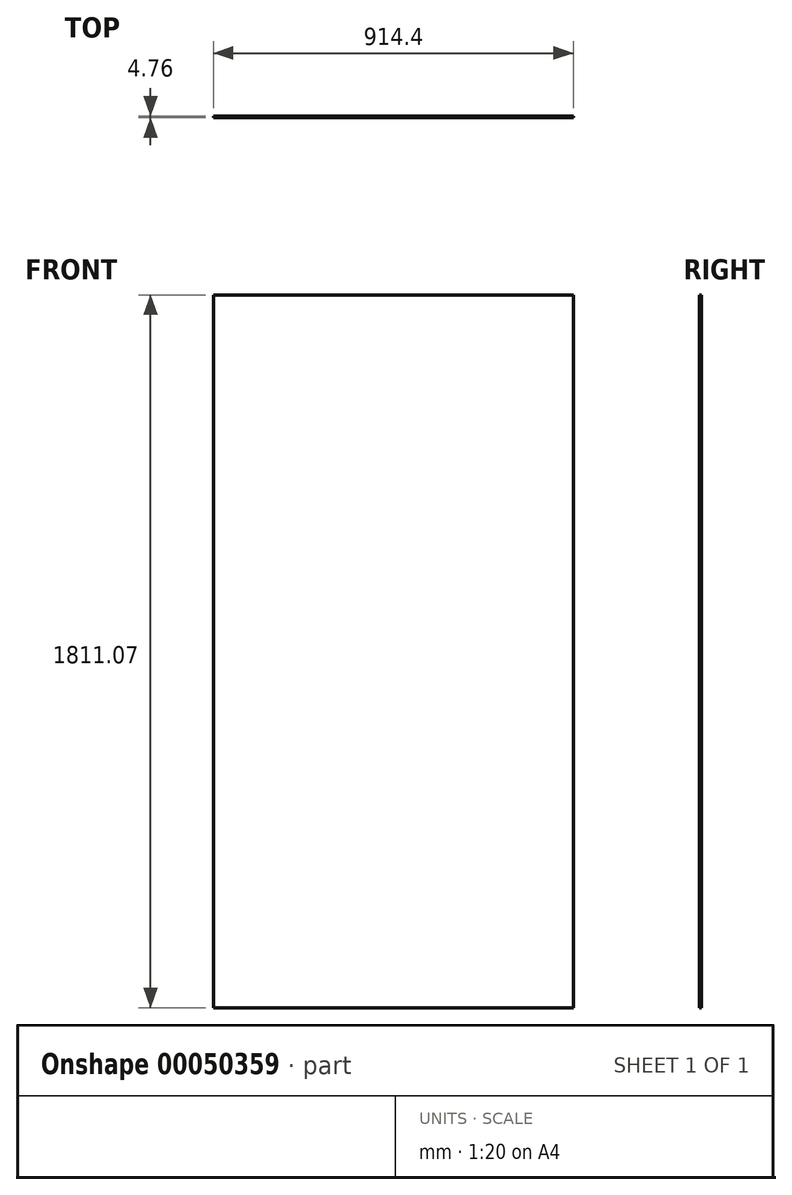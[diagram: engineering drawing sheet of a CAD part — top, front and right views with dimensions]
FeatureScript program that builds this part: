
annotation { "Feature Type Name" : "Feature", "Feature Type Description" : "" }
export const myFeature = defineFeature(function(context is Context, id is Id, definition is map)
    precondition{}
    {
        {
            var Q0;
            Q0=qCreatedBy(makeId("Front.planeOp"),FACE);
            var sketch = newSketch(context, id + "F0", { "sketchPlane" : qUnion([Q0])});
            skLineSegment(sketch, "E0.bottom", {"start": v(-465.1, 1463.78) * mm, "end": v(449.3, 1463.78) * mm});
            skLineSegment(sketch, "E0.top", {"start": v(-465.1, -347.3) * mm, "end": v(449.3, -347.3) * mm});
            skLineSegment(sketch, "E0.left", {"start": v(-465.1, 1463.78) * mm, "end": v(-465.1, -347.3) * mm});
            skLineSegment(sketch, "E0.right", {"start": v(449.3, 1463.78) * mm, "end": v(449.3, -347.3) * mm});
            skSolve(sketch);
        }
        {
            var Q0;
            Q0=makeQuery(id+"F0.imprint","IMPRINT",FACE,{"disambiguationData":[TD([[makeQuery(id+"F0.imprint","IMPRINT",EDGE,{"derivedFrom":sQuery(id+"F0.wireOp",EDGE,"E0.bottom")}),-1.0]])]});
            extrude(context, id + "F1", {"entities" : qUnion([Q0]), "depth" : 4.76 * mm});
        }
    });
